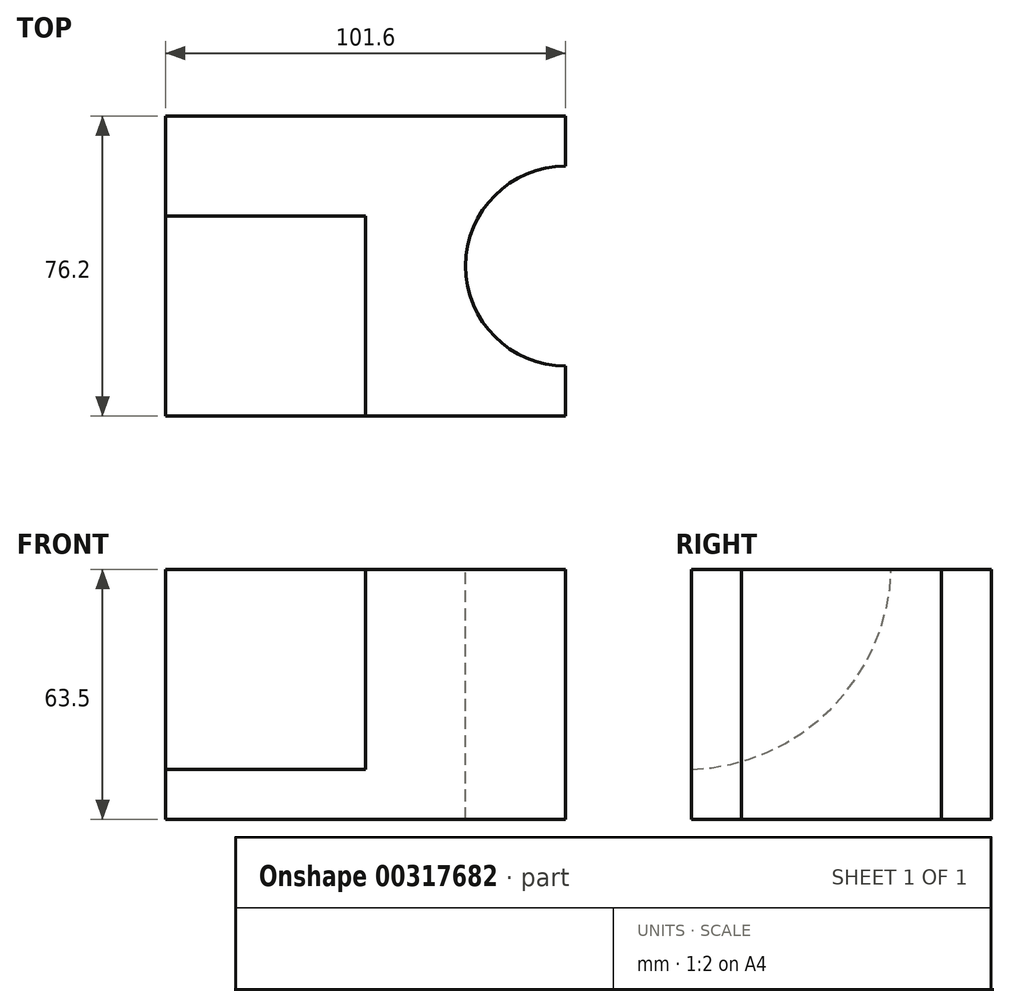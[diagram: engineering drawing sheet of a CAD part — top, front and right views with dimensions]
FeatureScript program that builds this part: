
annotation { "Feature Type Name" : "Feature", "Feature Type Description" : "" }
export const myFeature = defineFeature(function(context is Context, id is Id, definition is map)
    precondition{}
    {
        {
            var Q0;
            Q0=qCreatedBy(makeId("Front.planeOp"),FACE);
            var sketch = newSketch(context, id + "F0", { "sketchPlane" : qUnion([Q0])});
            skLineSegment(sketch, "E0", {"start": v(-52.2, -39.22) * mm, "end": v(49.4, -39.22) * mm});
            skLineSegment(sketch, "E1", {"start": v(49.4, -39.22) * mm, "end": v(49.4, 24.28) * mm});
            skLineSegment(sketch, "E2", {"start": v(49.4, 24.28) * mm, "end": v(-52.2, 24.28) * mm});
            skLineSegment(sketch, "E3", {"start": v(-52.2, 24.28) * mm, "end": v(-52.2, -39.22) * mm});
            skSolve(sketch);
        }
        {
            var Q0;
            Q0 = qSketchRegion(id + "F0", true);
            extrude(context, id + "F1", {"entities" : qUnion([Q0]), "depth" : 76.2 * mm});
        }
        {
            var Q0;
            Q0=makeQuery(id+"F1.opExtrude","SWEPT_FACE",FACE,{"disambiguationData":[OSD([sQuery(id+"F0.wireOp",EDGE,"E2")])]});
            var sketch = newSketch(context, id + "F2", { "sketchPlane" : qUnion([Q0])});
            skCircle(sketch, "E4", {"center": v(49.4, -38.1) * mm, "radius": 25.4 * mm});
            skLineSegment(sketch, "E5", {"start": v(49.4, -76.2) * mm, "end": v(49.4, -63.5) * mm});
            skLineSegment(sketch, "E6", {"start": v(49.4, -12.7) * mm, "end": v(49.4, -63.5) * mm});
            skSolve(sketch);
        }
        {
            var Q0;
            {var subQ0=sQuery(id+"F2.wireOp",EDGE,"E6");Q0=makeQuery(id+"F2.imprint","IMPRINT",FACE,{"disambiguationData":[TD([[makeQuery(id+"F2.imprint","IMPRINT",EDGE,{"derivedFrom":subQ0}),1.0]])]});}
            extrude(context, id + "F3", {"entities" : qUnion([Q0]), "operationType" : NewBodyOperationType.REMOVE, "oppositeDirection" : true, "depth" : 63.5 * mm});
        }
        {
            var Q0;
            Q0=makeQuery(id+"F1.opExtrude","SWEPT_FACE",FACE,{"disambiguationData":[OSD([sQuery(id+"F0.wireOp",EDGE,"E3")])]});
            var sketch = newSketch(context, id + "F4", { "sketchPlane" : qUnion([Q0])});
            skArc(sketch, "E7", {"start": v(25.4, 24.28) * mm, "mid": v(40.8, -11.12) * mm, "end": v(76.2, -26.52) * mm});
            skSolve(sketch);
        }
        {
            var Q0;
            {var subQ0=sQuery(id+"F4.wireOp",EDGE,"E7");Q0=makeQuery(id+"F4.imprint","IMPRINT",FACE,{"disambiguationData":[TD([[makeQuery(id+"F4.imprint","IMPRINT",EDGE,{"derivedFrom":subQ0}),1.0]])]});}
            extrude(context, id + "F5", {"entities" : qUnion([Q0]), "operationType" : NewBodyOperationType.REMOVE, "oppositeDirection" : true, "depth" : 50.8 * mm});
        }
    });
